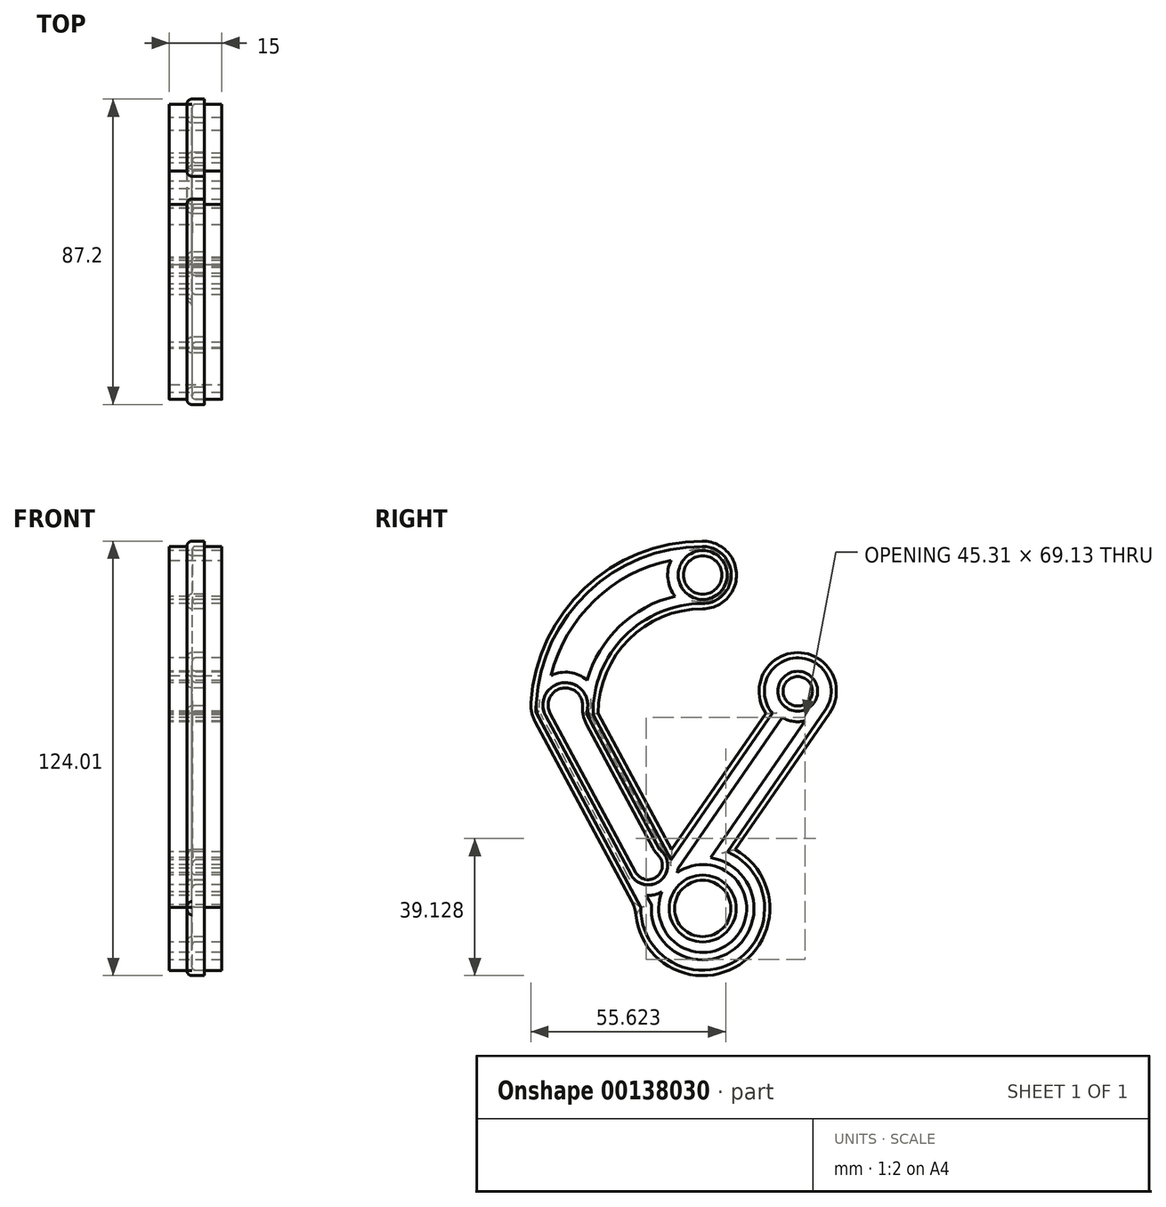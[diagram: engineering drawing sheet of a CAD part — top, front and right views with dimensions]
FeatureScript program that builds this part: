
annotation { "Feature Type Name" : "Feature", "Feature Type Description" : "" }
export const myFeature = defineFeature(function(context is Context, id is Id, definition is map)
    precondition{}
    {
        {
            var Q0;
            Q0=qCreatedBy(makeId("Right.planeOp"),FACE);
            var sketch = newSketch(context, id + "F7", { "sketchPlane" : qUnion([Q0])});
            skLineSegment(sketch, "E0", {"start": v(36.2, 0) * mm, "end": v(9.28, -38.97) * mm});
            skLineSegment(sketch, "E1", {"start": v(0, 48.67) * mm, "end": v(0, -55.4) * mm, "construction": true});
            skArc(sketch, "E2", {"start": v(-19.16, -55.74) * mm, "mid": v(9.73, -72.24) * mm, "end": v(9.28, -38.97) * mm});
            skLineSegment(sketch, "E3", {"start": v(-19.16, -55.74) * mm, "end": v(-49.11, 0) * mm});
            skArc(sketch, "E4", {"start": v(-49.11, 0) * mm, "mid": v(-34.76, 34.7) * mm, "end": v(-0.1, 49.11) * mm});
            skArc(sketch, "E5", {"start": v(-0.1, 49.11) * mm, "mid": v(9.65, 39.51) * mm, "end": v(0, 29.81) * mm});
            skArc(sketch, "E6", {"start": v(0, 29.81) * mm, "mid": v(-21.08, 21.08) * mm, "end": v(-29.81, 0) * mm});
            skLineSegment(sketch, "E7", {"start": v(-29.81, 0) * mm, "end": v(-8.87, -38.97) * mm});
            skLineSegment(sketch, "E8", {"start": v(-8.87, -38.97) * mm, "end": v(18.06, 0) * mm});
            skCircle(sketch, "E9", {"center": v(0, -55.74) * mm, "radius": 8.04 * mm});
            skCircle(sketch, "E10", {"center": v(0, 39.46) * mm, "radius": 5.48 * mm});
            skArc(sketch, "E11", {"start": v(36.2, 0) * mm, "mid": v(27.13, 17.3) * mm, "end": v(18.06, 0) * mm});
            skCircle(sketch, "E12", {"center": v(27.13, 6.27) * mm, "radius": 4.2 * mm});
            skLineSegment(sketch, "E13", {"start": v(-19.16, -45.35) * mm, "end": v(-43.53, 0) * mm});
            skLineSegment(sketch, "E14", {"start": v(-34.9, 0) * mm, "end": v(-13.4, -39.98) * mm});
            skArc(sketch, "E15", {"start": v(-34.9, 0) * mm, "mid": v(-39.21, 7.23) * mm, "end": v(-43.53, 0) * mm});
            skArc(sketch, "E16", {"start": v(-19.16, -45.35) * mm, "mid": v(-12.8, -46.4) * mm, "end": v(-13.4, -39.98) * mm});
            skSolve(sketch);
        }
        {
            var Q0;
            Q0=makeQuery(id+"F7.imprint","IMPRINT",FACE,{"disambiguationData":[TD([[makeQuery(id+"F7.imprint","IMPRINT",EDGE,{"derivedFrom":sQuery(id+"F7.wireOp",EDGE,"E0")}),-1.0]])]});
            extrude(context, id + "F0", {"entities" : qUnion([Q0]), "depth" : 5 * mm});
        }
        {
            var Q0;
            Q0=makeQuery(id+"F0.opExtrude","CAP_FACE",FACE,{"disambiguationData":[OSD([sQuery(id+"F7.wireOp",EDGE,"E0"),sQuery(id+"F7.wireOp",EDGE,"E2"),sQuery(id+"F7.wireOp",EDGE,"E3"),sQuery(id+"F7.wireOp",EDGE,"E4"),sQuery(id+"F7.wireOp",EDGE,"E5"),sQuery(id+"F7.wireOp",EDGE,"E6"),sQuery(id+"F7.wireOp",EDGE,"E7"),sQuery(id+"F7.wireOp",EDGE,"E8"),sQuery(id+"F7.wireOp",EDGE,"E9"),sQuery(id+"F7.wireOp",EDGE,"E10"),sQuery(id+"F7.wireOp",EDGE,"E11"),sQuery(id+"F7.wireOp",EDGE,"E12"),sQuery(id+"F7.wireOp",EDGE,"E13"),sQuery(id+"F7.wireOp",EDGE,"E14"),sQuery(id+"F7.wireOp",EDGE,"E15"),sQuery(id+"F7.wireOp",EDGE,"E16")])],"isStart":false});
            shell(context, id + "F1", {"entities" : qUnion([Q0]), "thickness" : 1.5 * mm});
        }
        {
            var Q0;
            {var subQ0=sQuery(id+"F7.wireOp",EDGE,"E16");var subQ1=sQuery(id+"F7.wireOp",EDGE,"E15");var subQ2=sQuery(id+"F7.wireOp",EDGE,"E14");var subQ3=sQuery(id+"F7.wireOp",EDGE,"E13");var subQ4=sQuery(id+"F7.wireOp",EDGE,"E12");var subQ5=sQuery(id+"F7.wireOp",EDGE,"E11");var subQ6=sQuery(id+"F7.wireOp",EDGE,"E10");var subQ7=sQuery(id+"F7.wireOp",EDGE,"E9");var subQ8=sQuery(id+"F7.wireOp",EDGE,"E8");var subQ9=sQuery(id+"F7.wireOp",EDGE,"E7");var subQ10=sQuery(id+"F7.wireOp",EDGE,"E6");var subQ11=sQuery(id+"F7.wireOp",EDGE,"E5");var subQ12=sQuery(id+"F7.wireOp",EDGE,"E4");var subQ13=sQuery(id+"F7.wireOp",EDGE,"E3");var subQ14=sQuery(id+"F7.wireOp",EDGE,"E2");var subQ15=sQuery(id+"F7.wireOp",EDGE,"E0");Q0=makeQuery(id+"F1.opShell","OFFSET_FACE",FACE,{"disambiguationData":[OSD([subQ15,subQ14,subQ13,subQ12,subQ11,subQ10,subQ9,subQ8,subQ7,subQ6,subQ5,subQ4,subQ3,subQ2,subQ1,subQ0]),TDD([makeQuery(id+"F0.opExtrude","CAP_FACE",FACE,{"disambiguationData":[OSD([subQ15,subQ14,subQ13,subQ12,subQ11,subQ10,subQ9,subQ8,subQ7,subQ6,subQ5,subQ4,subQ3,subQ2,subQ1,subQ0])],"isStart":true})])]});}
            fillet(context, id + "F2", {"entities" : qUnion([Q0]), "radius" : 1 * mm, "tangentPropagation" : true, "allowEdgeOverflow" : false});
        }
        {
            var Q0;
            Q0=makeQuery(id+"F0.opExtrude","CAP_EDGE",EDGE,{"disambiguationData":[OSD([sQuery(id+"F7.wireOp",EDGE,"E14")])],"isStart":true});
            var Q1;
            Q1=makeQuery(id+"F0.opExtrude","CAP_EDGE",EDGE,{"disambiguationData":[OSD([sQuery(id+"F7.wireOp",EDGE,"E15")])],"isStart":true});
            var Q2;
            Q2=makeQuery(id+"F0.opExtrude","CAP_EDGE",EDGE,{"disambiguationData":[OSD([sQuery(id+"F7.wireOp",EDGE,"E13")])],"isStart":true});
            var Q3;
            Q3=makeQuery(id+"F0.opExtrude","CAP_EDGE",EDGE,{"disambiguationData":[OSD([sQuery(id+"F7.wireOp",EDGE,"E16")])],"isStart":true});
            var Q4;
            Q4=makeQuery(id+"F0.opExtrude","CAP_EDGE",EDGE,{"disambiguationData":[OSD([sQuery(id+"F7.wireOp",EDGE,"E10")])],"isStart":true});
            var Q5;
            Q5=makeQuery(id+"F0.opExtrude","CAP_EDGE",EDGE,{"disambiguationData":[OSD([sQuery(id+"F7.wireOp",EDGE,"E12")])],"isStart":true});
            var Q6;
            Q6=makeQuery(id+"F0.opExtrude","CAP_EDGE",EDGE,{"disambiguationData":[OSD([sQuery(id+"F7.wireOp",EDGE,"E9")])],"isStart":true});
            var Q7;
            Q7=makeQuery(id+"F0.opExtrude","CAP_FACE",FACE,{"disambiguationData":[OSD([sQuery(id+"F7.wireOp",EDGE,"E0"),sQuery(id+"F7.wireOp",EDGE,"E2"),sQuery(id+"F7.wireOp",EDGE,"E3"),sQuery(id+"F7.wireOp",EDGE,"E4"),sQuery(id+"F7.wireOp",EDGE,"E5"),sQuery(id+"F7.wireOp",EDGE,"E6"),sQuery(id+"F7.wireOp",EDGE,"E7"),sQuery(id+"F7.wireOp",EDGE,"E8"),sQuery(id+"F7.wireOp",EDGE,"E9"),sQuery(id+"F7.wireOp",EDGE,"E10"),sQuery(id+"F7.wireOp",EDGE,"E11"),sQuery(id+"F7.wireOp",EDGE,"E12"),sQuery(id+"F7.wireOp",EDGE,"E13"),sQuery(id+"F7.wireOp",EDGE,"E14"),sQuery(id+"F7.wireOp",EDGE,"E15"),sQuery(id+"F7.wireOp",EDGE,"E16")])],"isStart":true});
            fillet(context, id + "F3", {"entities" : qUnion([Q0, Q1, Q2, Q3, Q4, Q5, Q6, Q7]), "radius" : 1.5 * mm, "tangentPropagation" : true, "allowEdgeOverflow" : false});
        }
        {
            var Q0;
            Q0=makeQuery(id+"F0.opExtrude","SWEPT_EDGE",EDGE,{"disambiguationData":[OSD([sQuery(id+"F7.wireOp",EDGE,"E3"),sQuery(id+"F7.wireOp",EDGE,"E4")])]});
            var Q1;
            Q1=makeQuery(id+"F0.opExtrude","SWEPT_EDGE",EDGE,{"disambiguationData":[OSD([sQuery(id+"F7.wireOp",EDGE,"E14"),sQuery(id+"F7.wireOp",EDGE,"E15")])]});
            var Q2;
            Q2=makeQuery(id+"F0.opExtrude","SWEPT_EDGE",EDGE,{"disambiguationData":[OSD([sQuery(id+"F7.wireOp",EDGE,"E14"),sQuery(id+"F7.wireOp",EDGE,"E16")])]});
            var Q3;
            Q3=makeQuery(id+"F0.opExtrude","SWEPT_EDGE",EDGE,{"disambiguationData":[OSD([sQuery(id+"F7.wireOp",EDGE,"E2"),sQuery(id+"F7.wireOp",EDGE,"E3")])]});
            fillet(context, id + "F4", {"entities" : qUnion([Q0, Q1, Q2, Q3]), "radius" : 10 * mm, "tangentPropagation" : true, "allowEdgeOverflow" : false});
        }
        {
            var Q0;
            Q0=makeQuery(id+"F0.opExtrude","CAP_FACE",FACE,{"disambiguationData":[OSD([sQuery(id+"F7.wireOp",EDGE,"E0"),sQuery(id+"F7.wireOp",EDGE,"E2"),sQuery(id+"F7.wireOp",EDGE,"E3"),sQuery(id+"F7.wireOp",EDGE,"E4"),sQuery(id+"F7.wireOp",EDGE,"E5"),sQuery(id+"F7.wireOp",EDGE,"E6"),sQuery(id+"F7.wireOp",EDGE,"E7"),sQuery(id+"F7.wireOp",EDGE,"E8"),sQuery(id+"F7.wireOp",EDGE,"E9"),sQuery(id+"F7.wireOp",EDGE,"E10"),sQuery(id+"F7.wireOp",EDGE,"E11"),sQuery(id+"F7.wireOp",EDGE,"E12"),sQuery(id+"F7.wireOp",EDGE,"E13"),sQuery(id+"F7.wireOp",EDGE,"E14"),sQuery(id+"F7.wireOp",EDGE,"E15"),sQuery(id+"F7.wireOp",EDGE,"E16")])],"isStart":true});
            extrude(context, id + "F5", {"entities" : qUnion([Q0]), "oppositeDirection" : true, "depth" : 10 * mm, "hasSecondDirection" : true, "secondDirectionOppositeDirection" : false, "secondDirectionDepth" : 5 * mm});
        }
        {
            var Q0;
            Q0=makeQuery(id+"F5.opExtrude","CAP_FACE",FACE,{"disambiguationData":[OSD([sQuery(id+"F7.wireOp",EDGE,"E0"),sQuery(id+"F7.wireOp",EDGE,"E2"),sQuery(id+"F7.wireOp",EDGE,"E3"),sQuery(id+"F7.wireOp",EDGE,"E4"),sQuery(id+"F7.wireOp",EDGE,"E5"),sQuery(id+"F7.wireOp",EDGE,"E6"),sQuery(id+"F7.wireOp",EDGE,"E7"),sQuery(id+"F7.wireOp",EDGE,"E8"),sQuery(id+"F7.wireOp",EDGE,"E9"),sQuery(id+"F7.wireOp",EDGE,"E10"),sQuery(id+"F7.wireOp",EDGE,"E11"),sQuery(id+"F7.wireOp",EDGE,"E12"),sQuery(id+"F7.wireOp",EDGE,"E13"),sQuery(id+"F7.wireOp",EDGE,"E14"),sQuery(id+"F7.wireOp",EDGE,"E15"),sQuery(id+"F7.wireOp",EDGE,"E16")])],"isStart":true});
            var Q1;
            Q1=makeQuery(id+"F5.opExtrude","CAP_FACE",FACE,{"disambiguationData":[OSD([sQuery(id+"F7.wireOp",EDGE,"E0"),sQuery(id+"F7.wireOp",EDGE,"E2"),sQuery(id+"F7.wireOp",EDGE,"E3"),sQuery(id+"F7.wireOp",EDGE,"E4"),sQuery(id+"F7.wireOp",EDGE,"E5"),sQuery(id+"F7.wireOp",EDGE,"E6"),sQuery(id+"F7.wireOp",EDGE,"E7"),sQuery(id+"F7.wireOp",EDGE,"E8"),sQuery(id+"F7.wireOp",EDGE,"E9"),sQuery(id+"F7.wireOp",EDGE,"E10"),sQuery(id+"F7.wireOp",EDGE,"E11"),sQuery(id+"F7.wireOp",EDGE,"E12"),sQuery(id+"F7.wireOp",EDGE,"E13"),sQuery(id+"F7.wireOp",EDGE,"E14"),sQuery(id+"F7.wireOp",EDGE,"E15"),sQuery(id+"F7.wireOp",EDGE,"E16")])],"isStart":false});
            shell(context, id + "F6", {"entities" : qUnion([Q0, Q1]), "thickness" : 3 * mm});
        }
    });
